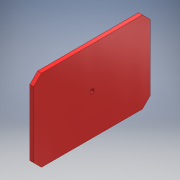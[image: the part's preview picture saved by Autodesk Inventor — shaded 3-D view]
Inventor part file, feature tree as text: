
AUTODESK INVENTOR PART (.ipt)
format: ipt  version: 2017 SP1 (Build 210196100, 196)  size: 105,984 bytes
history: native  units: mm
features: extrude x2, sketch x2, chamfer x1
ambient origin geometry x8: Origin, YZ Plane, XZ Plane, XY Plane, X Axis, Y Axis, Z Axis, Center Point
bodies: Solid1 (feature_tree)
feature tree (5):
  extrude  "Extrusion1"  Depth=42.0mm
  chamfer  "Chamfer1"  Distance=2.0mm
  extrude  "Extrusion2"  Depth=2.0mm
  sketch  "Sketch1"  dims[d0=60.0mm d1=42.0mm d2=2.0mm d3=0.0mm]
  sketch  "Sketch2"  dims[d4=4.0mm d5=2.0mm d6=45.0deg d7=2.0mm d8=2.0mm d9=0.0mm]
